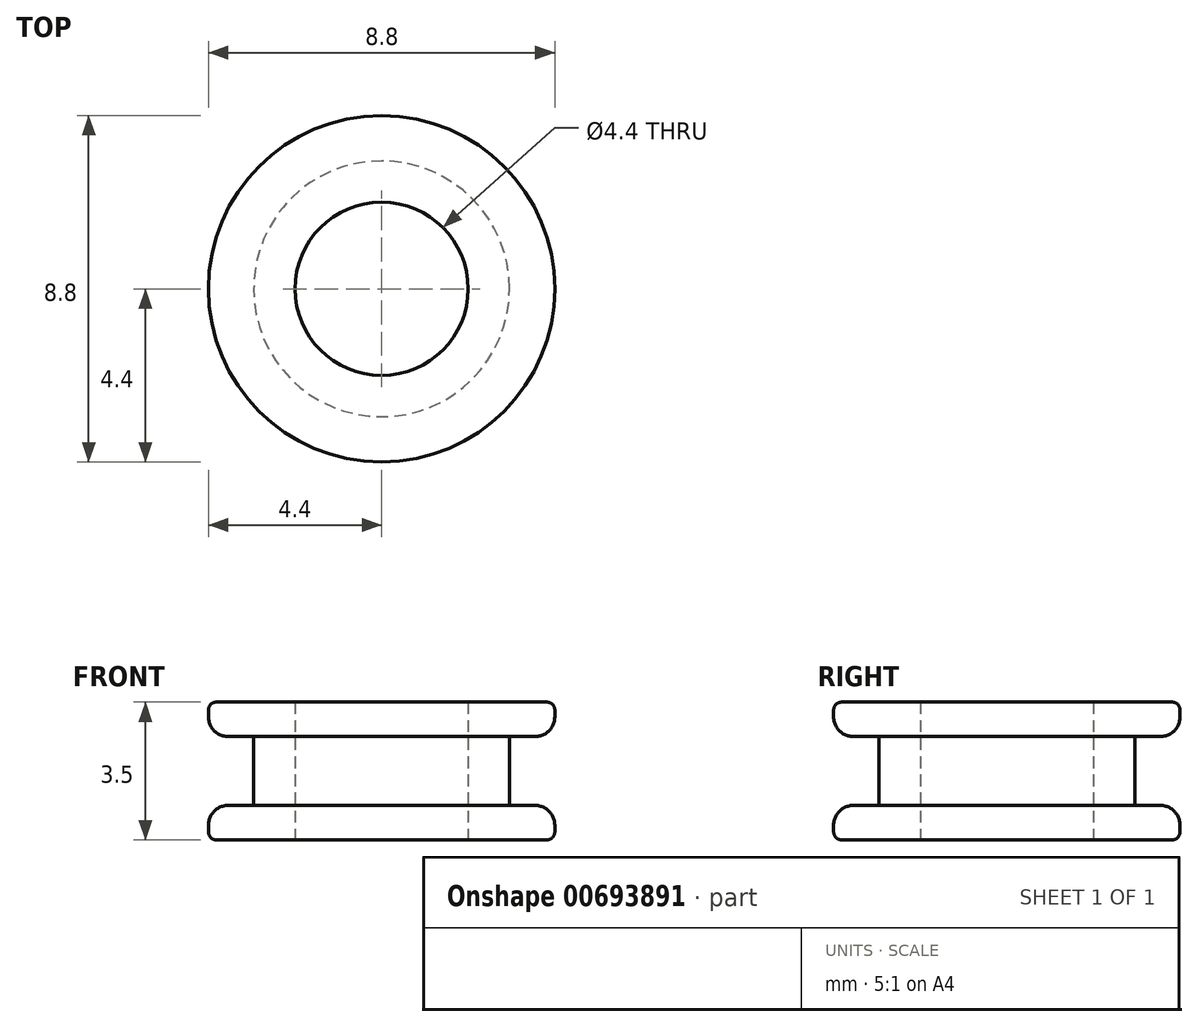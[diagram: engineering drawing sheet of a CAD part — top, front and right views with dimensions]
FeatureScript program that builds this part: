
annotation { "Feature Type Name" : "Feature", "Feature Type Description" : "" }
export const myFeature = defineFeature(function(context is Context, id is Id, definition is map)
    precondition{}
    {
        {
            var Q0;
            Q0=qCreatedBy(makeId("Front.planeOp"),FACE);
            var sketch = newSketch(context, id + "F0", { "sketchPlane" : qUnion([Q0])});
            skLineSegment(sketch, "E0", {"start": v(4.2, 3.5) * mm, "end": v(2.2, 3.5) * mm});
            skLineSegment(sketch, "E1", {"start": v(4.4, 0.2) * mm, "end": v(4.4, 0.37) * mm});
            skLineSegment(sketch, "E2", {"start": v(4.4, 3.3) * mm, "end": v(4.4, 3.13) * mm});
            skLineSegment(sketch, "E3", {"start": v(3.9, 2.63) * mm, "end": v(3.25, 2.63) * mm});
            skLineSegment(sketch, "E4", {"start": v(3.9, 0.87) * mm, "end": v(3.25, 0.87) * mm});
            skLineSegment(sketch, "E5", {"start": v(3.25, 2.63) * mm, "end": v(3.25, 0.87) * mm});
            skPoint(sketch, "E6.visualSharp", {"position": v(4.4, 2.63) * mm});
            skArc(sketch, "E6.filletArc", {"start": v(3.9, 2.63) * mm, "mid": v(4.25, 2.77) * mm, "end": v(4.4, 3.13) * mm});
            skPoint(sketch, "E7.visualSharp", {"position": v(4.4, 0.88) * mm});
            skArc(sketch, "E7.filletArc", {"start": v(4.4, 0.37) * mm, "mid": v(4.25, 0.73) * mm, "end": v(3.9, 0.87) * mm});
            skLineSegment(sketch, "E8", {"start": v(2.2, 0) * mm, "end": v(2.2, 3.5) * mm});
            skPoint(sketch, "E8.endSnap0", {"position": v(2.2, 3.5) * mm});
            skPoint(sketch, "E9.visualSharp", {"position": v(4.4, 3.5) * mm});
            skArc(sketch, "E9.filletArc", {"start": v(4.4, 3.3) * mm, "mid": v(4.34, 3.44) * mm, "end": v(4.2, 3.5) * mm});
            skPoint(sketch, "E10.visualSharp", {"position": v(4.4, 0) * mm});
            skArc(sketch, "E10.filletArc", {"start": v(4.2, 0) * mm, "mid": v(4.34, 0.06) * mm, "end": v(4.4, 0.2) * mm});
            skLineSegment(sketch, "E11", {"start": v(2.2, 0) * mm, "end": v(4.2, 0) * mm});
            skLineSegment(sketch, "E12", {"start": v(0, 0) * mm, "end": v(0, 3.37) * mm});
            skSolve(sketch);
        }
        {
            var Q0;
            Q0 = qSketchRegion(id + "F0", true);
            var Q1;
            Q1=sQuery(id+"F0.wireOp",EDGE,"E12");
            revolve(context, id + "F1", {"entities" : qUnion([Q0]), "axis" : qUnion([Q1]), "revolveType" : RevolveType.FULL});
        }
    });
